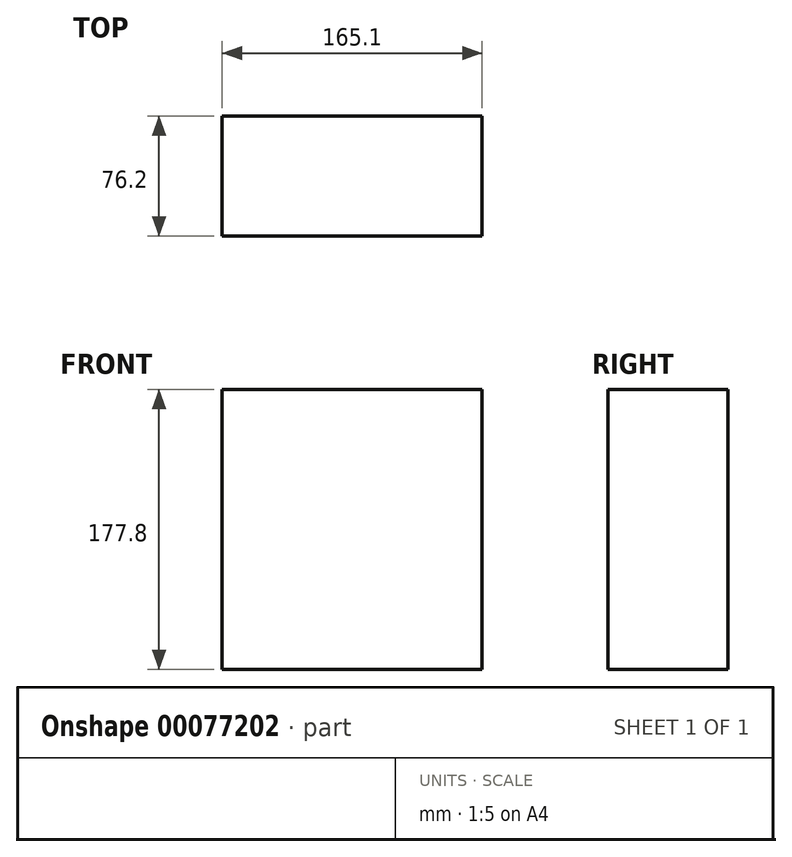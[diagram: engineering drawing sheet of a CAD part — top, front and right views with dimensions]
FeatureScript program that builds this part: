
annotation { "Feature Type Name" : "Feature", "Feature Type Description" : "" }
export const myFeature = defineFeature(function(context is Context, id is Id, definition is map)
    precondition{}
    {
        {
            var Q0;
            Q0=qCreatedBy(makeId("Front.planeOp"),FACE);
            var sketch = newSketch(context, id + "F0", { "sketchPlane" : qUnion([Q0])});
            skLineSegment(sketch, "E0.bottom", {"start": v(-75.07, 92.35) * mm, "end": v(90.03, 92.35) * mm});
            skLineSegment(sketch, "E0.top", {"start": v(-75.07, -85.45) * mm, "end": v(90.03, -85.45) * mm});
            skLineSegment(sketch, "E0.left", {"start": v(-75.07, 92.35) * mm, "end": v(-75.07, -85.45) * mm});
            skLineSegment(sketch, "E0.right", {"start": v(90.03, 92.35) * mm, "end": v(90.03, -85.45) * mm});
            skSolve(sketch);
        }
        {
            var Q0;
            Q0 = qSketchRegion(id + "F0", true);
            extrude(context, id + "F1", {"entities" : qUnion([Q0]), "depth" : 76.2 * mm});
        }
    });
